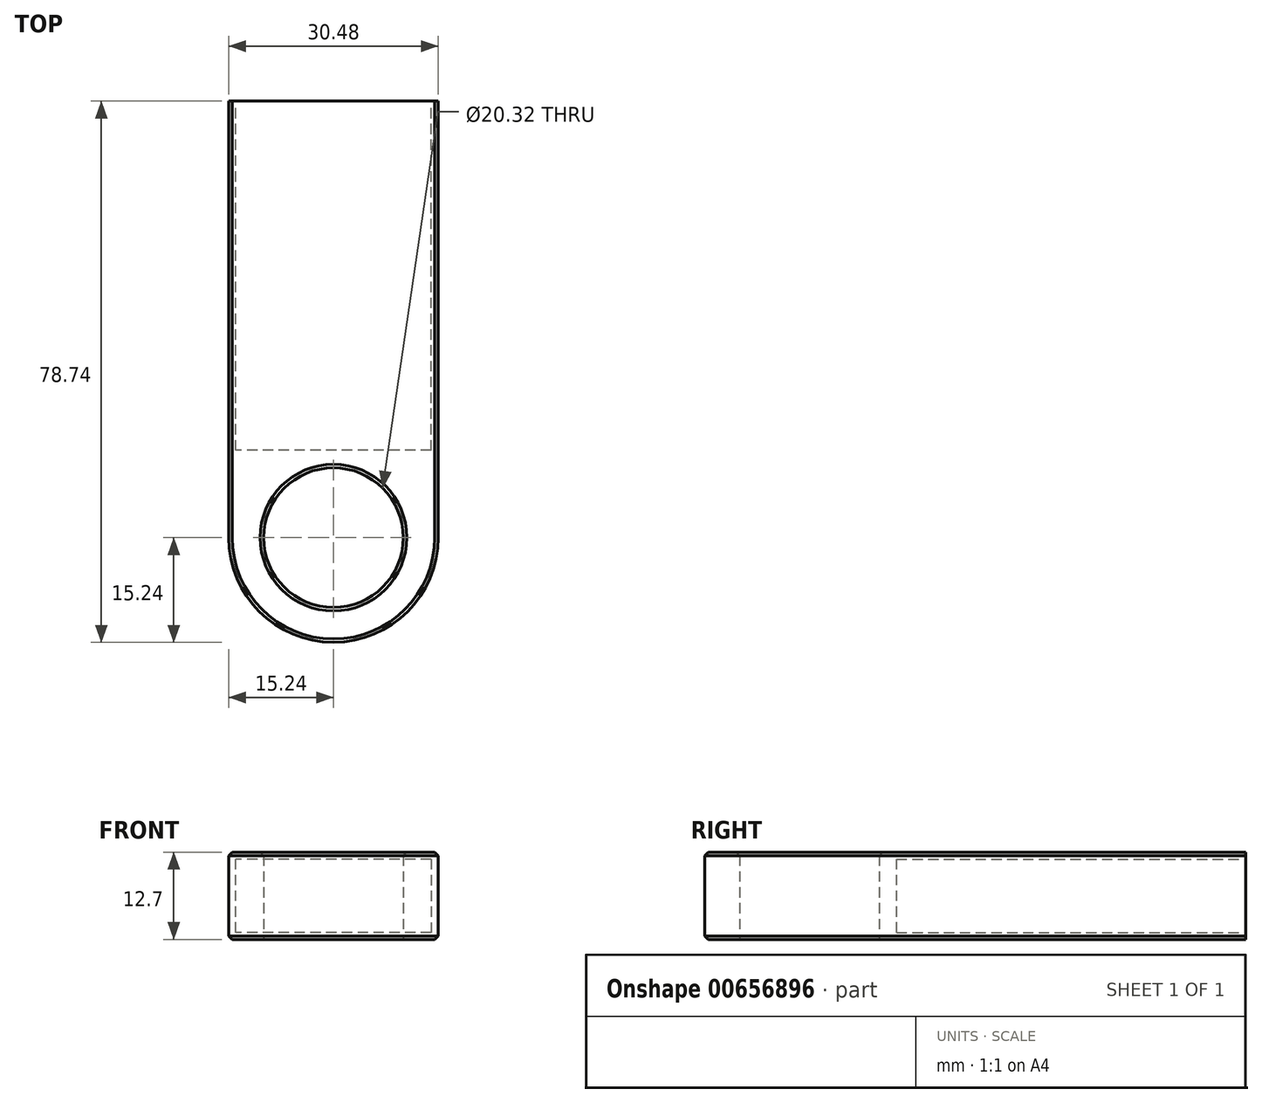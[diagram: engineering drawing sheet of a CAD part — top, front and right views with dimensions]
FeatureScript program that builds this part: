
annotation { "Feature Type Name" : "Feature", "Feature Type Description" : "" }
export const myFeature = defineFeature(function(context is Context, id is Id, definition is map)
    precondition{}
    {
        {
            var Q0;
            Q0=qCreatedBy(makeId("Top.planeOp"),FACE);
            var sketch = newSketch(context, id + "F0", { "sketchPlane" : qUnion([Q0])});
            skLineSegment(sketch, "E0.bottom", {"start": v(15.24, 31.75) * mm, "end": v(-15.24, 31.75) * mm});
            skLineSegment(sketch, "E0.top", {"start": v(15.24, -31.75) * mm, "end": v(-15.24, -31.75) * mm});
            skLineSegment(sketch, "E0.left", {"start": v(15.24, 31.75) * mm, "end": v(15.24, -31.75) * mm});
            skLineSegment(sketch, "E0.right", {"start": v(-15.24, 31.75) * mm, "end": v(-15.24, -31.75) * mm});
            skPoint(sketch, "E0.middle", {"position": v(0, 0) * mm});
            skLineSegment(sketch, "E1", {"start": v(0, 0) * mm, "end": v(0, -31.75) * mm});
            skCircle(sketch, "E2", {"center": v(0, -31.75) * mm, "radius": 15.24 * mm});
            skSolve(sketch);
        }
        {
            var Q0;
            Q0 = qSketchRegion(id + "F0", true);
            extrude(context, id + "F1", {"entities" : qUnion([Q0]), "depth" : 12.7 * mm, "offsetDistance" : 25.4 * mm});
        }
        {
            var Q0;
            Q0=qCreatedBy(makeId("Top.planeOp"),FACE);
            var sketch = newSketch(context, id + "F2", { "sketchPlane" : qUnion([Q0])});
            skLineSegment(sketch, "E3", {"start": v(0, 0) * mm, "end": v(0, -31.75) * mm});
            skLineSegment(sketch, "E4", {"start": v(0, -31.75) * mm, "end": v(10.16, -31.75) * mm});
            skCircle(sketch, "E5", {"center": v(0, -31.75) * mm, "radius": 10.16 * mm});
            skSolve(sketch);
        }
        {
            var Q0;
            Q0 = qSketchRegion(id + "F2", true);
            extrude(context, id + "F3", {"entities" : qUnion([Q0]), "operationType" : NewBodyOperationType.REMOVE, "depth" : 25.4 * mm, "offsetDistance" : 25.4 * mm});
        }
        {
            var Q0;
            Q0=makeQuery(id+"F1.opExtrude","CAP_EDGE",EDGE,{"disambiguationData":[OSD([sQuery(id+"F0.wireOp",EDGE,"E0.right")])],"isStart":false});
            var Q1;
            Q1=makeQuery(id+"F1.opExtrude","CAP_EDGE",EDGE,{"disambiguationData":[OSD([sQuery(id+"F0.wireOp",EDGE,"E0.right")])],"isStart":true});
            var Q2;
            Q2=makeQuery(id+"F3.boolean.opBoolean","INTERSECT",EDGE,{"derivedFrom":[makeQuery(id+"F1.opExtrude","CAP_FACE",FACE,{"disambiguationData":[OSD([sQuery(id+"F0.wireOp",EDGE,"E0.bottom"),sQuery(id+"F0.wireOp",EDGE,"E0.left"),sQuery(id+"F0.wireOp",EDGE,"E0.right"),sQuery(id+"F0.wireOp",EDGE,"E2")])],"isStart":false}),makeQuery(id+"F3.opExtrude","SWEPT_FACE",FACE,{"disambiguationData":[OSD([sQuery(id+"F2.wireOp",EDGE,"E5")])]})]});
            var Q3;
            Q3=makeQuery(id+"F3.boolean.opBoolean","COPY",EDGE,{"derivedFrom":makeQuery(id+"F3.opExtrude","CAP_EDGE",EDGE,{"disambiguationData":[OSD([sQuery(id+"F2.wireOp",EDGE,"E5")])],"isStart":true})});
            chamfer(context, id + "F4", {"entities" : qUnion([Q0, Q1, Q2, Q3]), "width" : 0.5 * mm, "tangentPropagation" : true});
        }
        {
            var Q0;
            Q0=qCreatedBy(makeId("Front.planeOp"),FACE);
            cPlane(context, id + "F5", {"entities" : qUnion([Q0]), "cplaneType" : CPlaneType.OFFSET, "offset" : 31.75 * mm, "oppositeDirection" : true, "width" : 152.4 * mm, "height" : 152.4 * mm});
        }
        {
            var Q0;
            Q0=qCreatedBy(id+"F5.planeOp",FACE);
            var sketch = newSketch(context, id + "F6", { "sketchPlane" : qUnion([Q0])});
            skLineSegment(sketch, "E6", {"start": v(0, 0) * mm, "end": v(0, 1) * mm});
            skLineSegment(sketch, "E7", {"start": v(0, 1) * mm, "end": v(-14.23, 1) * mm});
            skLineSegment(sketch, "E8", {"start": v(-14.23, 1) * mm, "end": v(-14.23, 11.67) * mm});
            skLineSegment(sketch, "E9.bottom", {"start": v(-14.23, 11.67) * mm, "end": v(0, 11.67) * mm});
            skLineSegment(sketch, "E9.top", {"start": v(-14.23, 1) * mm, "end": v(0, 1) * mm});
            skLineSegment(sketch, "E9.left", {"start": v(-14.23, 11.67) * mm, "end": v(-14.23, 1) * mm});
            skLineSegment(sketch, "E9.right", {"start": v(0, 11.67) * mm, "end": v(0, 1) * mm});
            skLineSegment(sketch, "E10.MirrorCS", {"start": v(14.23, 11.67) * mm, "end": v(0, 11.67) * mm});
            skLineSegment(sketch, "E11.MirrorCS", {"start": v(14.23, 11.67) * mm, "end": v(14.23, 1) * mm});
            skLineSegment(sketch, "E12.MirrorCS", {"start": v(14.23, 1) * mm, "end": v(0, 1) * mm});
            skSolve(sketch);
        }
        {
            var Q0;
            Q0=makeQuery(id+"F6.imprint","IMPRINT",FACE,{"disambiguationData":[TD([[makeQuery(id+"F6.imprint","IMPRINT",EDGE,{"derivedFrom":sQuery(id+"F6.wireOp",EDGE,"E9.right")}),1.0]])]});
            var Q1;
            Q1=makeQuery(id+"F6.imprint","IMPRINT",FACE,{"disambiguationData":[TD([[makeQuery(id+"F6.imprint","IMPRINT",EDGE,{"derivedFrom":sQuery(id+"F6.wireOp",EDGE,"E9.bottom")}),-1.0]])]});
            extrude(context, id + "F7", {"entities" : qUnion([Q0, Q1]), "operationType" : NewBodyOperationType.REMOVE, "depth" : 50.8 * mm, "offsetDistance" : 25.4 * mm});
        }
    });
